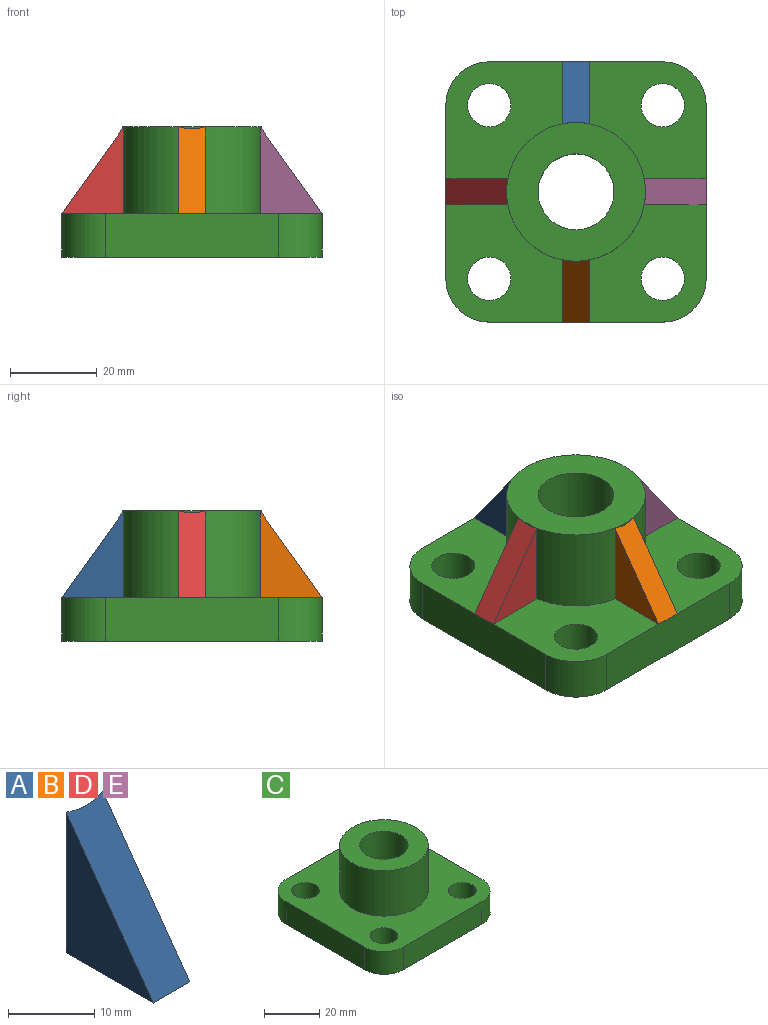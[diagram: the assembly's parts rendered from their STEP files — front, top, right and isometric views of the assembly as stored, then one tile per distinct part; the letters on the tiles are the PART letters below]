
ASSEMBLY  parts=5 mates=1
PART A: 5 faces, bbox 6x14.3x20 mm
  f0: plane 14.28x6mm, normal (0,0,-1), area 84.6mm2, adj f1,f2,f3,f4
  f1: plane 20x14.28mm, normal (1,0,0), area 142.8mm2, adj f0,f3,f4
  f2: plane 20x14.28mm, normal (-1,0,0), area 142.8mm2, adj f0,f3,f4
  f3: plane 20x14.28mm, normal (0,-0.81,0.58), area 145.5mm2, adj f0,f1,f2,f4
  f4: cylinder r=16mm len=20mm, axis (0,0,-1), area 119.1mm2, adj f0,f1,f2,f3
PART B: same geometry as A
PART C: 17 faces, bbox 60x60x30 mm
  f0: plane 40x10mm, normal (1,0,0), area 400mm2, adj f4,f5,f6,f9
  f1: plane 40x10mm, normal (0,1,0), area 400mm2, adj f4,f5,f6,f7
  f2: plane 40x10mm, normal (-1,0,0), area 400mm2, adj f4,f5,f7,f8
  f3: plane 40x10mm, normal (0,-1,0), area 400mm2, adj f4,f5,f8,f9
  f4: plane 60x60mm, normal (0,0,1), area 2395.8mm2, adj f0,f1,f2,f3,f6,f7,f8,f9
  f5: plane 60x60mm, normal (0,0,-1), area 2959.5mm2, adj f0,f1,f2,f3,f6,f7,f8,f9
  f6: cylinder r=10mm len=10mm, axis (0,0,1), area 157.1mm2, adj f0,f1,f4,f5
  f7: cylinder r=10mm len=10mm, axis (0,0,-1), area 157.1mm2, adj f1,f2,f4,f5
  f8: cylinder r=10mm len=10mm, axis (0,0,1), area 157.1mm2, adj f2,f3,f4,f5
  f9: cylinder r=10mm len=10mm, axis (0,0,-1), area 157.1mm2, adj f0,f3,f4,f5
  f10: cylinder r=16mm len=32mm, axis (0,0,-1), area 2010.6mm2, adj f4,f11
  f11: plane 32x32mm, normal (0,0,1), area 563.7mm2, adj f10,f16
  f12: cylinder r=5mm len=10mm, axis (0,0,1), area 314.2mm2, adj f4,f5
  f13: cylinder r=5mm len=10mm, axis (0,0,1), area 314.2mm2, adj f4,f5
  f14: cylinder r=5mm len=10mm, axis (0,0,1), area 314.2mm2, adj f4,f5
  f15: cylinder r=5mm len=10mm, axis (0,0,1), area 314.2mm2, adj f4,f5
  f16: cylinder r=8.75mm len=30mm, axis (0,0,1), area 1649.3mm2, adj f5,f11
PART D: same geometry as A
PART E: same geometry as A
PLACE A rot(axis=(0,0,1),180deg) t=(-0.3,35.61,14.39)mm
PLACE B t=(-0.3,-10.11,14.39)mm
PLACE C t=(-0.3,12.75,4.39)mm
PLACE D rot(axis=(0,0,-1),90deg) t=(-23.16,12.75,14.39)mm
PLACE E rot(axis=(0,0,1),90deg) t=(22.56,12.75,14.39)mm
MATE fastened B.f0 <-> C.f4  axis (0,0,-1) through (-0.3,-17.25,14.39)mm
